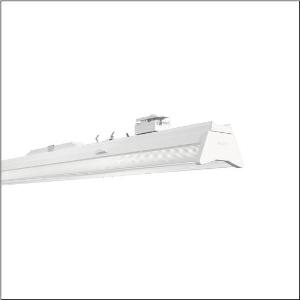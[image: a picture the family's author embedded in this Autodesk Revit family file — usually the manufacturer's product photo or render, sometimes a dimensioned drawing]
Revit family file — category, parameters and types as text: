
# Revit family: licross_21_performance_mo_52td16dn4a5g
name_source: partatom
category: Lighting Fixtures
units: mm (PartAtom-declared; Revit-internal decimal feet)

## family parameters
Cut with Voids When Loaded = No
Host = Face
Light Source = No
Part Type = Normal
Room Calculation Point = No
Round Connector Dimension = Use Diameter
Shared = No

## types (1)
- --- (1 x LED, 10840 lm, 62 W, 4000K)
    Apparent Load = 62 VA
    CIE Flux Codes = 66 88 96 79 100
    Color Rendering = 80
    Color Temperature = 4000K
    Default Elevation = 1800 mm
    Description = Licross 21 Performance MO, luminaire insert, of sheet steel, galvanised, coil coated, white, length: 1.500mm, width: 120mm, height: 123mm, LED rated luminous flux: 10.840lm, light colour: 840, SDCM (Standard Deviation of Colour Matching)MacAdam ≤ 3 SDCM (initial), control gear: DALI 2, with plug, 5-pole, with phase selection, mains connection: 220..240V, AC, 50/60Hz, rated input power: 62W, internal wiring halogen-free, primary light control with lens, of plastic, primary optical cover: cover, of PMMA, light emission: direct/indirect distribution, primary light characteristic: symmetric, protection rating (complete): IP54, insulation class (complete): insulation class I (protective earthing), certification: CE, ENEC, VDE, UKCA, protection symbol: D if used in an environment with non-conductive dust loads with corresponding accessories, impact resistance: IK06, permissible ambient temperature for indoor applications: -25..+35°C, corresponds to IFS (International Featured Standards) requirements for safety and quality in the food industry, reducing of maximum allowable ambient temperature of 5°C with ceiling mounting, LABS conformity tested according to VDMA 24364:2018-05, The light source and the operating device comply with the requirements of the Ecodesign Regulation (EU) 2019/2020 and are replaceable in accordance with this regulation, packaging unit: 1 piece
    Height = 114 mm
    Lamp = 1 x LED
    Lamp Light Flux = 10840 lm
    Lamp Power = 62 W
    Lamp count = 1
    Length = 1500 mm
    Luminous efficacy = 175 lm/W
    Manufacturer = Siteco
    ModVariant = No
    Model = 52TD16DN4A5G
    Mounting Place = Ceiling
    Mounting Type = Pendant
    Number of Poles = 1
    OnlyDefault = Yes
    Power Factor = 1
    Product Name = Licross 21 Performance MO
    Product group = luminaire insert | ceiling pendant
    ProductGroupID = 901
    Protection Class = Protection class I
    Protection Degree = IP 54
    RLX_Detail_Level = 1
    RLX_Emergency_Light_Flux = 0 lm
    RLX_Emergency_Type = 0
    RLX_Emergency_Type_DB = No
    RlxData = <blob elided: 34377 chars, md5=b7d482ce>
    Socket = socket
    Standby Power = 0 W
    System Light Flux = 10840 lm
    System Power = 62 W
    Type Comments = factory setting: luminous flux: 100 % | dim-lin: 254 | 418 mA
    Type Image = l_1256138.jpg
    URL = http://relux.com
    VarID = @adj_130869
    Voltage = 0 V
    Weight = 0.00 kg
    Width = 120 mm

## geometry (parser evidence)
native form markers: Blend x4, Sweep x12
no freeform markers — native parametric forms only
